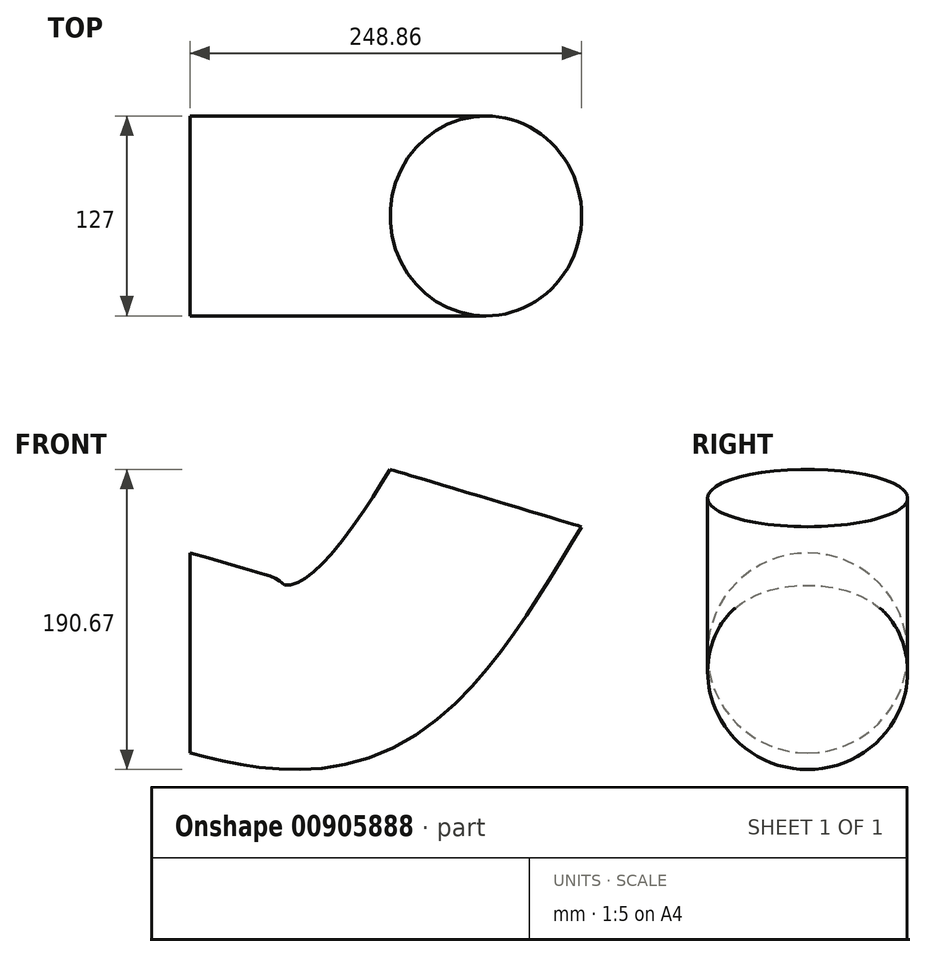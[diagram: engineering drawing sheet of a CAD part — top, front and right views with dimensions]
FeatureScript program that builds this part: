
annotation { "Feature Type Name" : "Feature", "Feature Type Description" : "" }
export const myFeature = defineFeature(function(context is Context, id is Id, definition is map)
    precondition{}
    {
        {
            var Q0;
            Q0=qCreatedBy(makeId("Right.planeOp"),FACE);
            var sketch = newSketch(context, id + "F0", { "sketchPlane" : qUnion([Q0])});
            skCircle(sketch, "E0", {"center": v(0, 0) * mm, "radius": 63.5 * mm});
            skSolve(sketch);
        }
        {
            var Q0;
            Q0=qCreatedBy(makeId("Front.planeOp"),FACE);
            var sketch = newSketch(context, id + "F1", { "sketchPlane" : qUnion([Q0])});
            skFitSpline(sketch, "E1", {"points": [v(0, 0) * mm, v(97.86, -6.05) * mm, v(188.03, 98.4) * mm], "startDerivative": vector(224.87, -60.26) * mm, "endDerivative": vector(153.22, 248.3) * mm});
            skSolve(sketch);
        }
        {
            var Q0;
            Q0=makeQuery(id+"F0.imprint","IMPRINT",FACE,{"disambiguationData":[TD([[makeQuery(id+"F0.imprint","IMPRINT",EDGE,{"derivedFrom":sQuery(id+"F0.wireOp",EDGE,"E0")}),1.0]])]});
            var Q1;
            Q1=sQuery(id+"F1.wireOp",EDGE,"E1");
            sweep(context, id + "F2", {"profiles" : qUnion([Q0]), "path" : qUnion([Q1])});
        }
    });
